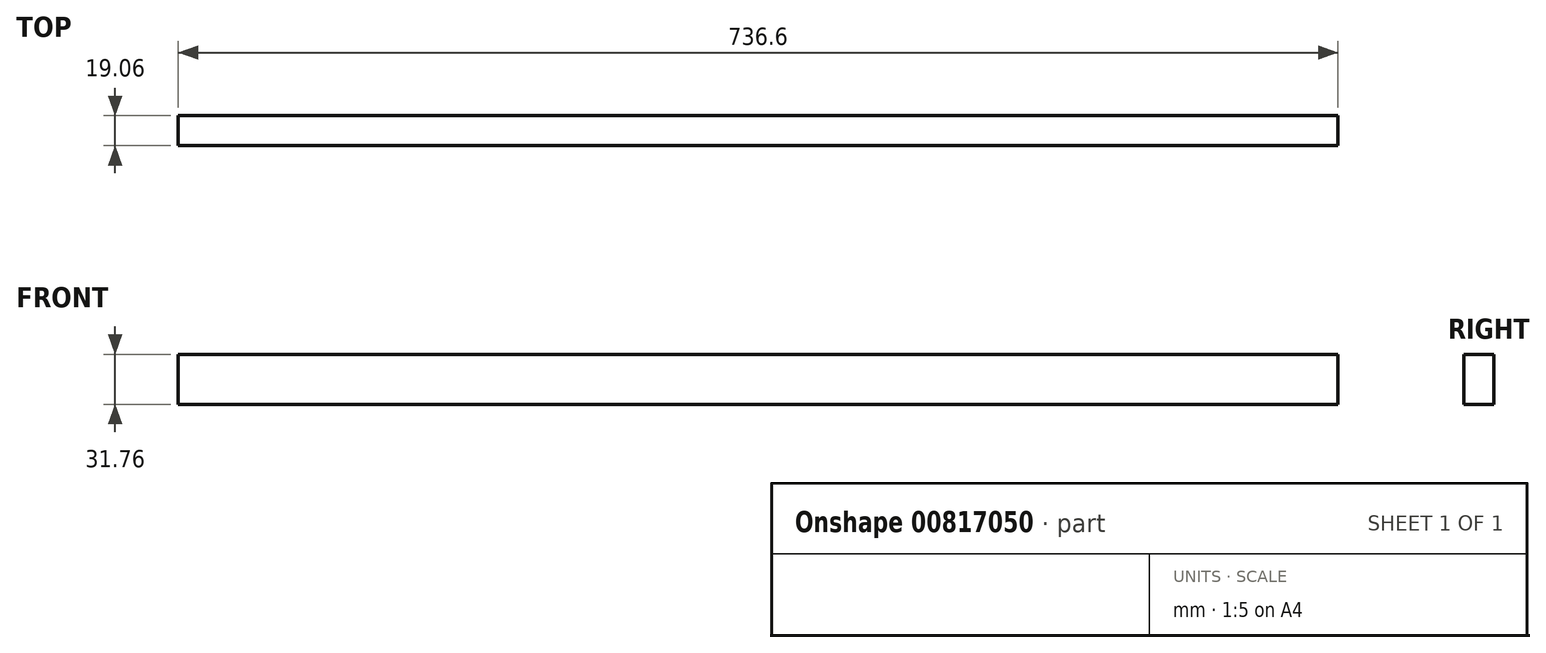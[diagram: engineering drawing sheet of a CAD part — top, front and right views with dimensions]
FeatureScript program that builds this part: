
annotation { "Feature Type Name" : "Feature", "Feature Type Description" : "" }
export const myFeature = defineFeature(function(context is Context, id is Id, definition is map)
    precondition{}
    {
        {
            var Q0;
            Q0=qCreatedBy(makeId("Right.planeOp"),FACE);
            var sketch = newSketch(context, id + "F0", { "sketchPlane" : qUnion([Q0])});
            skLineSegment(sketch, "E0.bottom", {"start": v(9.52, 15.88) * mm, "end": v(-9.52, 15.88) * mm});
            skLineSegment(sketch, "E0.top", {"start": v(9.52, -15.88) * mm, "end": v(-9.52, -15.88) * mm});
            skLineSegment(sketch, "E0.left", {"start": v(9.53, 15.88) * mm, "end": v(9.52, -15.88) * mm});
            skLineSegment(sketch, "E0.right", {"start": v(-9.52, 15.88) * mm, "end": v(-9.53, -15.88) * mm});
            skPoint(sketch, "E0.middle", {"position": v(0, 0) * mm});
            skSolve(sketch);
        }
        {
            var Q0;
            Q0 = qSketchRegion(id + "F0", true);
            extrude(context, id + "F1", {"entities" : qUnion([Q0]), "depth" : 736.6 * mm, "offsetDistance" : 25.4 * mm});
        }
    });
